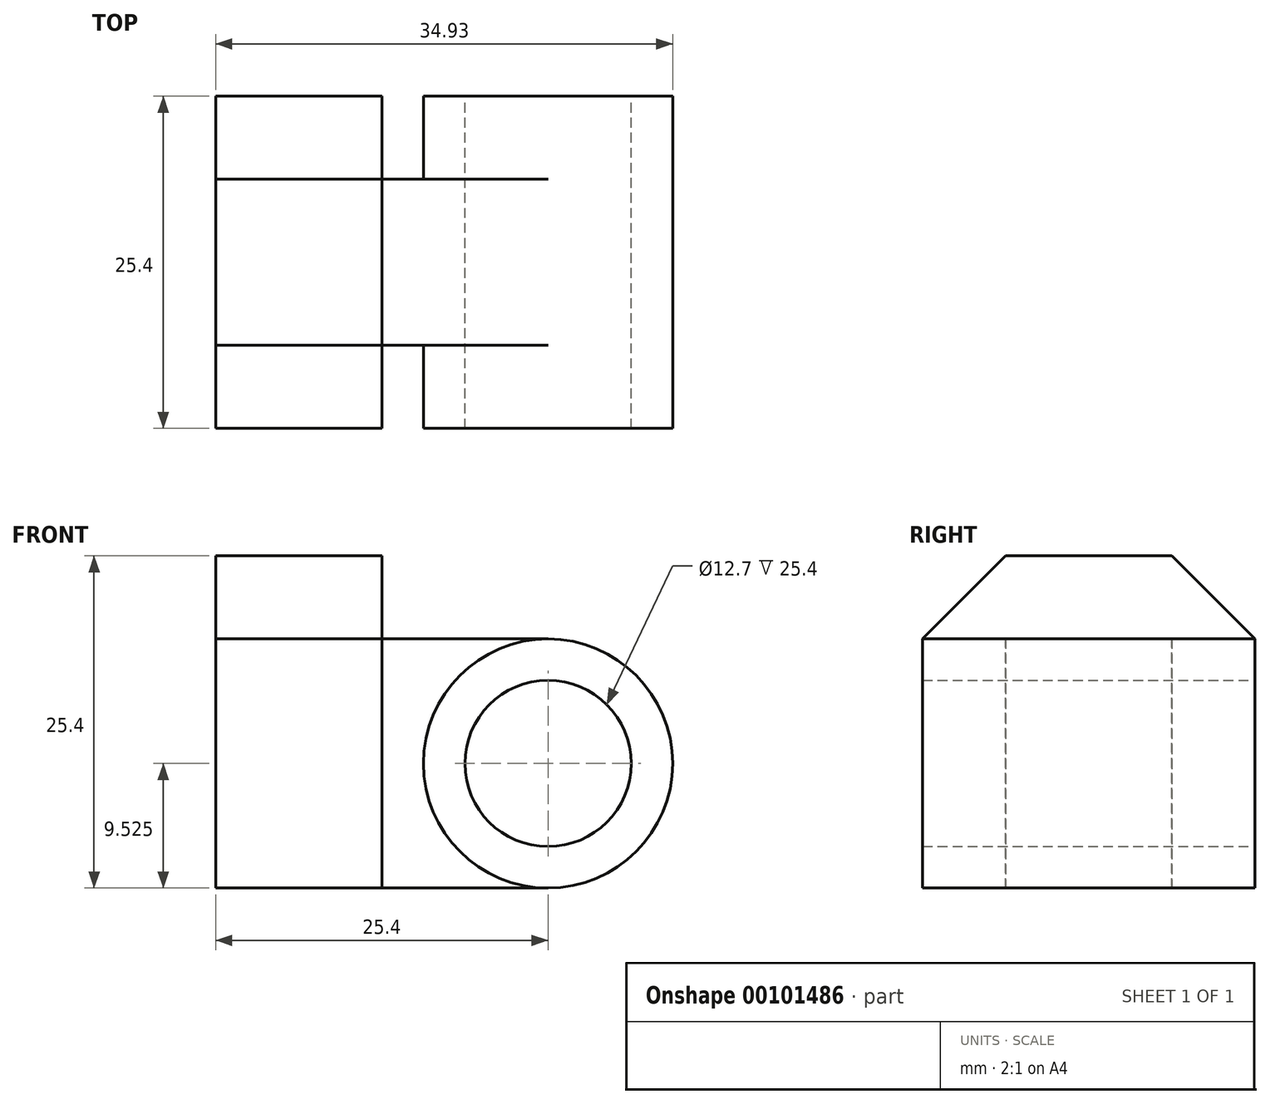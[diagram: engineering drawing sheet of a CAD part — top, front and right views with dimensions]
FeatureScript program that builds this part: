
annotation { "Feature Type Name" : "Feature", "Feature Type Description" : "" }
export const myFeature = defineFeature(function(context is Context, id is Id, definition is map)
    precondition{}
    {
        {
            var Q0;
            Q0=qCreatedBy(makeId("Right.planeOp"),FACE);
            var sketch = newSketch(context, id + "F0", { "sketchPlane" : qUnion([Q0])});
            skLineSegment(sketch, "E0", {"start": v(0, 0) * mm, "end": v(0, 19.05) * mm});
            skLineSegment(sketch, "E1", {"start": v(0, 19.05) * mm, "end": v(-6.35, 25.4) * mm});
            skLineSegment(sketch, "E2", {"start": v(-6.35, 25.4) * mm, "end": v(-19.05, 25.4) * mm});
            skLineSegment(sketch, "E3", {"start": v(-19.05, 25.4) * mm, "end": v(-25.4, 19.05) * mm});
            skLineSegment(sketch, "E4", {"start": v(-25.4, 19.05) * mm, "end": v(-25.4, 0) * mm});
            skLineSegment(sketch, "E5", {"start": v(-25.4, 0) * mm, "end": v(0, 0) * mm});
            skSolve(sketch);
        }
        {
            var Q0;
            Q0=makeQuery(id+"F0.imprint","IMPRINT",FACE,{"disambiguationData":[TD([[makeQuery(id+"F0.imprint","IMPRINT",EDGE,{"derivedFrom":sQuery(id+"F0.wireOp",EDGE,"E0")}),1.0]])]});
            extrude(context, id + "F1", {"entities" : qUnion([Q0]), "oppositeDirection" : true, "depth" : 12.7 * mm});
        }
        {
            var Q0;
            Q0=qCreatedBy(makeId("Front.planeOp"),FACE);
            var sketch = newSketch(context, id + "F2", { "sketchPlane" : qUnion([Q0])});
            skLineSegment(sketch, "E6", {"start": v(0, 0) * mm, "end": v(12.7, 0) * mm});
            skLineSegment(sketch, "E7", {"start": v(0, 0) * mm, "end": v(0, 19.05) * mm});
            skLineSegment(sketch, "E8", {"start": v(0, 19.05) * mm, "end": v(12.7, 19.05) * mm});
            skArc(sketch, "E9", {"start": v(12.7, 19.05) * mm, "mid": v(3.18, 9.52) * mm, "end": v(12.7, 0) * mm});
            skSolve(sketch);
        }
        {
            var Q0;
            Q0=makeQuery(id+"F2.imprint","IMPRINT",FACE,{"disambiguationData":[TD([[makeQuery(id+"F2.imprint","IMPRINT",EDGE,{"derivedFrom":sQuery(id+"F2.wireOp",EDGE,"E6")}),1.0]])]});
            extrude(context, id + "F3", {"entities" : qUnion([Q0]), "operationType" : NewBodyOperationType.ADD, "depth" : 19.05 * mm, "hasSecondDirection" : true, "secondDirectionOppositeDirection" : false, "secondDirectionDepth" : 6.35 * mm});
        }
        {
            var Q0;
            Q0=qCreatedBy(makeId("Front.planeOp"),FACE);
            var sketch = newSketch(context, id + "F4", { "sketchPlane" : qUnion([Q0])});
            skCircle(sketch, "E10", {"center": v(12.7, 9.53) * mm, "radius": 9.53 * mm});
            skPoint(sketch, "E10.first.point", {"position": v(12.7, 19.05) * mm});
            skPoint(sketch, "E10.second.point", {"position": v(12.7, 0) * mm});
            skCircle(sketch, "E11", {"center": v(12.7, 9.53) * mm, "radius": 6.35 * mm});
            skSolve(sketch);
        }
        {
            var Q0;
            Q0=makeQuery(id+"F4.imprint","IMPRINT",FACE,{"disambiguationData":[TD([[makeQuery(id+"F4.imprint","IMPRINT",EDGE,{"derivedFrom":sQuery(id+"F4.wireOp",EDGE,"E10")}),1.0]])]});
            extrude(context, id + "F5", {"entities" : qUnion([Q0]), "operationType" : NewBodyOperationType.ADD, "depth" : 25.4 * mm});
        }
    });
